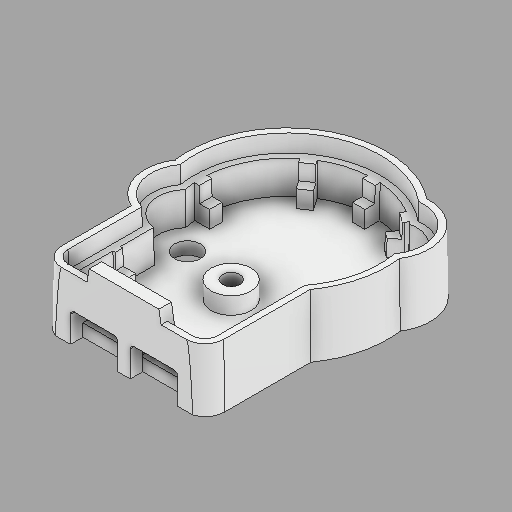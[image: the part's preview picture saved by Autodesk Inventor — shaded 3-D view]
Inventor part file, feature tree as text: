
AUTODESK INVENTOR PART (.ipt)
format: ipt  version: 2024.2 (Build 282272000, 272)  size: 262,144 bytes
history: native  units: in
note: dims shown in document units (in); Inventor stores cm internally (conversion verified against a paired STEP export)
features: fillet x1
ambient origin geometry x8: Origin, YZ Plane, XZ Plane, XY Plane, X Axis, Y Axis, Z Axis, Center Point
bodies: Solid1 (feature_tree)
feature tree (1):
  fillet  "Fillet3"  [1 undecoded]
note: 1 required parameter value undecoded (feature->parameter linkage not recoverable at this tier; creation-order binding heuristic only, values carry confidence <= 0.55)
